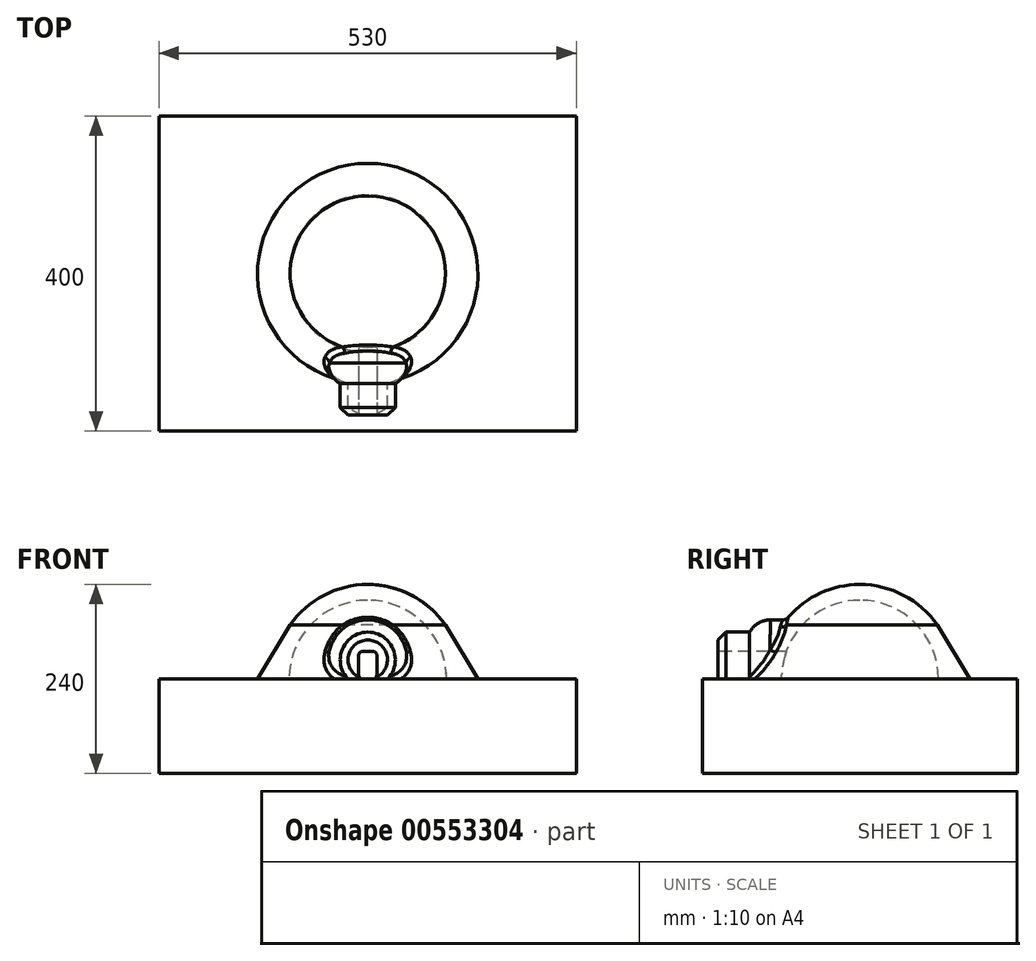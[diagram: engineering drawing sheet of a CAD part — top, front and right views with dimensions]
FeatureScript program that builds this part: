
annotation { "Feature Type Name" : "Feature", "Feature Type Description" : "" }
export const myFeature = defineFeature(function(context is Context, id is Id, definition is map)
    precondition{}
    {
        {
            var Q0;
            Q0=qCreatedBy(makeId("Front.planeOp"),FACE);
            var sketch = newSketch(context, id + "F0", { "sketchPlane" : qUnion([Q0])});
            skArc(sketch, "E0", {"start": v(-106.34, 55.6) * mm, "mid": v(-62.16, 102.65) * mm, "end": v(0, 120) * mm});
            skLineSegment(sketch, "E1", {"start": v(-98.57, 68.44) * mm, "end": v(-140, 0) * mm});
            skLineSegment(sketch, "E2", {"start": v(-140, 0) * mm, "end": v(-100, 0) * mm});
            skArc(sketch, "E3", {"start": v(-100, 0) * mm, "mid": v(-70.71, 70.71) * mm, "end": v(0, 100) * mm});
            skLineSegment(sketch, "E4", {"start": v(0, 120) * mm, "end": v(0, 100) * mm});
            skPoint(sketch, "E5.orphan", {"position": v(-120, 0) * mm});
            skSolve(sketch);
        }
        {
            var Q0;
            {var subQ0=sQuery(id+"F0.wireOp",EDGE,"E2");Q0=makeQuery(id+"F0.imprint","IMPRINT",FACE,{"disambiguationData":[TD([[makeQuery(id+"F0.imprint","IMPRINT",EDGE,{"derivedFrom":subQ0}),1.0]])]});}
            var Q1;
            Q1=sQuery(id+"F0.wireOp",EDGE,"E4");
            revolve(context, id + "F1", {"entities" : qUnion([Q0]), "axis" : qUnion([Q1]), "revolveType" : RevolveType.FULL});
        }
        {
            var Q0;
            Q0=qCreatedBy(makeId("Front.planeOp"),FACE);
            var sketch = newSketch(context, id + "F2", { "sketchPlane" : qUnion([Q0])});
            skArc(sketch, "E6", {"start": v(25.1, 0) * mm, "mid": v(0, 59.4) * mm, "end": v(-25.1, 0) * mm});
            skLineSegment(sketch, "E7", {"start": v(-128.93, 0) * mm, "end": v(130.21, 0) * mm, "construction": true});
            skPoint(sketch, "E8", {"position": v(-25.1, 0) * mm});
            skPoint(sketch, "E9", {"position": v(25.1, 0) * mm});
            skLineSegment(sketch, "E10", {"start": v(-25.1, 0) * mm, "end": v(25.1, 0) * mm});
            skSolve(sketch);
        }
        {
            var Q0;
            Q0 = qSketchRegion(id + "F2", true);
            extrude(context, id + "F3", {"entities" : qUnion([Q0]), "operationType" : NewBodyOperationType.ADD, "depth" : 180 * mm, "offsetDistance" : 25 * mm});
        }
        {
            var Q0;
            Q0=qCreatedBy(makeId("Front.planeOp"),FACE);
            var sketch = newSketch(context, id + "F4", { "sketchPlane" : qUnion([Q0])});
            skArc(sketch, "E11", {"start": v(43.3, 0) * mm, "mid": v(0, 75) * mm, "end": v(-43.3, 0) * mm});
            skLineSegment(sketch, "E12", {"start": v(-43.3, 0) * mm, "end": v(43.3, 0) * mm});
            skSolve(sketch);
        }
        {
            var Q0;
            Q0 = qSketchRegion(id + "F4", true);
            extrude(context, id + "F5", {"entities" : qUnion([Q0]), "operationType" : NewBodyOperationType.ADD, "depth" : 140 * mm, "offsetDistance" : 25 * mm});
        }
        {
            var Q0;
            Q0 = qSketchRegion(id + "F4", true);
            var Q1;
            Q1=makeQuery(id+"F1.opRevolve","SWEPT_FACE",FACE,{"disambiguationData":[OSD([sQuery(id+"F0.wireOp",EDGE,"E3")])]});
            extrude(context, id + "F6", {"entities" : qUnion([Q0]), "operationType" : NewBodyOperationType.REMOVE, "endBound" : BoundingType.UP_TO_SURFACE, "depth" : 25 * mm, "endBoundEntityFace" : qUnion([Q1]), "offsetDistance" : 25 * mm});
        }
        {
            var Q0;
            Q0=makeQuery(id+"F5.opExtrude","CAP_EDGE",EDGE,{"disambiguationData":[OSD([sQuery(id+"F4.wireOp",EDGE,"E11")])],"isStart":false});
            fillet(context, id + "F7", {"entities" : qUnion([Q0]), "radius" : 30 * mm, "tangentPropagation" : true, "allowEdgeOverflow" : false});
        }
        {
            var Q0;
            Q0=makeQuery(id+"F3.opExtrude","CAP_EDGE",EDGE,{"disambiguationData":[OSD([sQuery(id+"F2.wireOp",EDGE,"E6")])],"isStart":false});
            chamfer(context, id + "F8", {"entities" : qUnion([Q0]), "width" : 10 * mm, "tangentPropagation" : true});
        }
        {
            var Q0;
            Q0=makeQuery(id+"F5.boolean.opBoolean","INTERSECT",EDGE,{"derivedFrom":[makeQuery(id+"F1.opRevolve","SWEPT_FACE",FACE,{"disambiguationData":[OSD([sQuery(id+"F0.wireOp",EDGE,"E0")])]}),makeQuery(id+"F5.opExtrude","SWEPT_FACE",FACE,{"disambiguationData":[OSD([sQuery(id+"F4.wireOp",EDGE,"E11")])]})]});
            var Q1;
            Q1=makeQuery(id+"F5.boolean.opBoolean","INTERSECT",EDGE,{"disambiguationData":[OD(0.0)],"derivedFrom":[makeQuery(id+"F1.opRevolve","SWEPT_FACE",FACE,{"disambiguationData":[OSD([sQuery(id+"F0.wireOp",EDGE,"E1")])]}),makeQuery(id+"F5.opExtrude","SWEPT_FACE",FACE,{"disambiguationData":[OSD([sQuery(id+"F4.wireOp",EDGE,"E11")])]})]});
            var Q2;
            Q2=makeQuery(id+"F7.opFillet","BLEND_EDGE",EDGE,{"disambiguationData":[OD(1.0)],"blendedFrom":[makeQuery(id+"F5.opExtrude","CAP_EDGE",EDGE,{"disambiguationData":[OSD([sQuery(id+"F4.wireOp",EDGE,"E11")])],"isStart":false}),makeQuery(id+"F1.opRevolve","SWEPT_FACE",FACE,{"disambiguationData":[OSD([sQuery(id+"F0.wireOp",EDGE,"E1")])]})],"blendedInto":[makeQuery(id+"F1.opRevolve","SWEPT_FACE",FACE,{"disambiguationData":[OSD([sQuery(id+"F0.wireOp",EDGE,"E1")])]})]});
            var Q3;
            Q3=makeQuery(id+"F5.boolean.opBoolean","INTERSECT",EDGE,{"disambiguationData":[OD(1.0)],"derivedFrom":[makeQuery(id+"F1.opRevolve","SWEPT_FACE",FACE,{"disambiguationData":[OSD([sQuery(id+"F0.wireOp",EDGE,"E1")])]}),makeQuery(id+"F5.opExtrude","SWEPT_FACE",FACE,{"disambiguationData":[OSD([sQuery(id+"F4.wireOp",EDGE,"E11")])]})]});
            var Q4;
            Q4=makeQuery(id+"F7.opFillet","BLEND_EDGE",EDGE,{"disambiguationData":[OD(0.0)],"blendedFrom":[makeQuery(id+"F5.opExtrude","CAP_EDGE",EDGE,{"disambiguationData":[OSD([sQuery(id+"F4.wireOp",EDGE,"E11")])],"isStart":false}),makeQuery(id+"F1.opRevolve","SWEPT_FACE",FACE,{"disambiguationData":[OSD([sQuery(id+"F0.wireOp",EDGE,"E1")])]})],"blendedInto":[makeQuery(id+"F1.opRevolve","SWEPT_FACE",FACE,{"disambiguationData":[OSD([sQuery(id+"F0.wireOp",EDGE,"E1")])]})]});
            fillet(context, id + "F9", {"entities" : qUnion([Q0, Q1, Q2, Q3, Q4]), "radius" : 10 * mm, "tangentPropagation" : true, "allowEdgeOverflow" : false});
        }
        {
            var Q0;
            Q0=qCreatedBy(makeId("Top.planeOp"),FACE);
            var sketch = newSketch(context, id + "F10", { "sketchPlane" : qUnion([Q0])});
            skLineSegment(sketch, "E13.bottom", {"start": v(-265, 200) * mm, "end": v(265, 200) * mm});
            skLineSegment(sketch, "E13.top", {"start": v(-265, -200) * mm, "end": v(265, -200) * mm});
            skLineSegment(sketch, "E13.left", {"start": v(-265, 200) * mm, "end": v(-265, -200) * mm});
            skLineSegment(sketch, "E13.right", {"start": v(265, 200) * mm, "end": v(265, -200) * mm});
            skLineSegment(sketch, "E14", {"start": v(0, 334.35) * mm, "end": v(0, -312.82) * mm, "construction": true});
            skLineSegment(sketch, "E15", {"start": v(-393.58, 0) * mm, "end": v(403.64, 0) * mm, "construction": true});
            skSolve(sketch);
        }
        {
            var Q0;
            Q0 = qSketchRegion(id + "F10", true);
            extrude(context, id + "F11", {"entities" : qUnion([Q0]), "operationType" : NewBodyOperationType.ADD, "oppositeDirection" : true, "depth" : 120 * mm, "offsetDistance" : 25 * mm});
        }
        {
            var Q0;
            Q0=qCreatedBy(makeId("Front.planeOp"),FACE);
            var sketch = newSketch(context, id + "F12", { "sketchPlane" : qUnion([Q0])});
            skArc(sketch, "E16", {"start": v(-100, 0) * mm, "mid": v(-70.71, -70.71) * mm, "end": v(0, -100) * mm});
            skLineSegment(sketch, "E17", {"start": v(0, 0) * mm, "end": v(0, -100) * mm});
            skLineSegment(sketch, "E18", {"start": v(-100, 0) * mm, "end": v(0, 0) * mm});
            skPoint(sketch, "E19.orphan", {"position": v(0, 100) * mm});
            skSolve(sketch);
        }
        {
            var Q0;
            Q0=makeQuery(id+"F3.opExtrude","CAP_FACE",FACE,{"disambiguationData":[OSD([sQuery(id+"F2.wireOp",EDGE,"E6"),sQuery(id+"F2.wireOp",EDGE,"E10")])],"isStart":false});
            var sketch = newSketch(context, id + "F13", { "sketchPlane" : qUnion([Q0])});
            skLineSegment(sketch, "E20.bottom", {"start": v(-11.5, 0) * mm, "end": v(11.5, 0) * mm});
            skLineSegment(sketch, "E20.top", {"start": v(-11.5, 35) * mm, "end": v(11.5, 35) * mm});
            skLineSegment(sketch, "E20.left", {"start": v(-11.5, 0) * mm, "end": v(-11.5, 35) * mm});
            skLineSegment(sketch, "E20.right", {"start": v(11.5, 0) * mm, "end": v(11.5, 35) * mm});
            skSolve(sketch);
        }
        {
            var Q0;
            Q0 = qSketchRegion(id + "F13", true);
            extrude(context, id + "F14", {"entities" : qUnion([Q0]), "operationType" : NewBodyOperationType.REMOVE, "endBound" : BoundingType.UP_TO_NEXT, "oppositeDirection" : true, "depth" : 25 * mm, "offsetDistance" : 25 * mm});
        }
        {
            var Q0;
            Q0=qCreatedBy(makeId("Right.planeOp"),FACE);
            var sketch = newSketch(context, id + "F15", { "sketchPlane" : qUnion([Q0])});
            skLineSegment(sketch, "E21.bottom", {"start": v(211.34, 172.81) * mm, "end": v(-207.87, 172.81) * mm});
            skLineSegment(sketch, "E21.top", {"start": v(211.34, -176.52) * mm, "end": v(-207.87, -176.52) * mm});
            skLineSegment(sketch, "E21.left", {"start": v(211.34, 172.81) * mm, "end": v(211.34, -176.52) * mm});
            skLineSegment(sketch, "E21.right", {"start": v(-207.87, 172.81) * mm, "end": v(-207.87, -176.52) * mm});
            skSolve(sketch);
        }
        {
            var Q0;
            Q0=makeQuery(id+"F14.boolean.opBoolean","COPY",EDGE,{"derivedFrom":makeQuery(id+"F14.opExtrude","SWEPT_EDGE",EDGE,{"disambiguationData":[OSD([sQuery(id+"F13.wireOp",EDGE,"E20.top"),sQuery(id+"F13.wireOp",EDGE,"E20.left")])]})});
            var Q1;
            Q1=makeQuery(id+"F14.boolean.opBoolean","COPY",EDGE,{"derivedFrom":makeQuery(id+"F14.opExtrude","SWEPT_EDGE",EDGE,{"disambiguationData":[OSD([sQuery(id+"F13.wireOp",EDGE,"E20.top"),sQuery(id+"F13.wireOp",EDGE,"E20.right")])]})});
            var Q2;
            Q2=makeQuery(id+"F14.boolean.opBoolean","COPY",EDGE,{"derivedFrom":makeQuery(id+"F14.opExtrude","SWEPT_EDGE",EDGE,{"disambiguationData":[OSD([sQuery(id+"F2.wireOp",EDGE,"E10"),sQuery(id+"F13.wireOp",EDGE,"E20.bottom"),sQuery(id+"F13.wireOp",EDGE,"E20.left")])]})});
            var Q3;
            Q3=makeQuery(id+"F14.boolean.opBoolean","COPY",EDGE,{"derivedFrom":makeQuery(id+"F14.opExtrude","SWEPT_EDGE",EDGE,{"disambiguationData":[OSD([sQuery(id+"F2.wireOp",EDGE,"E10"),sQuery(id+"F13.wireOp",EDGE,"E20.bottom"),sQuery(id+"F13.wireOp",EDGE,"E20.right")])]})});
            fillet(context, id + "F16", {"entities" : qUnion([Q0, Q1, Q2, Q3]), "radius" : 5 * mm, "tangentPropagation" : true, "allowEdgeOverflow" : false});
        }
    });
